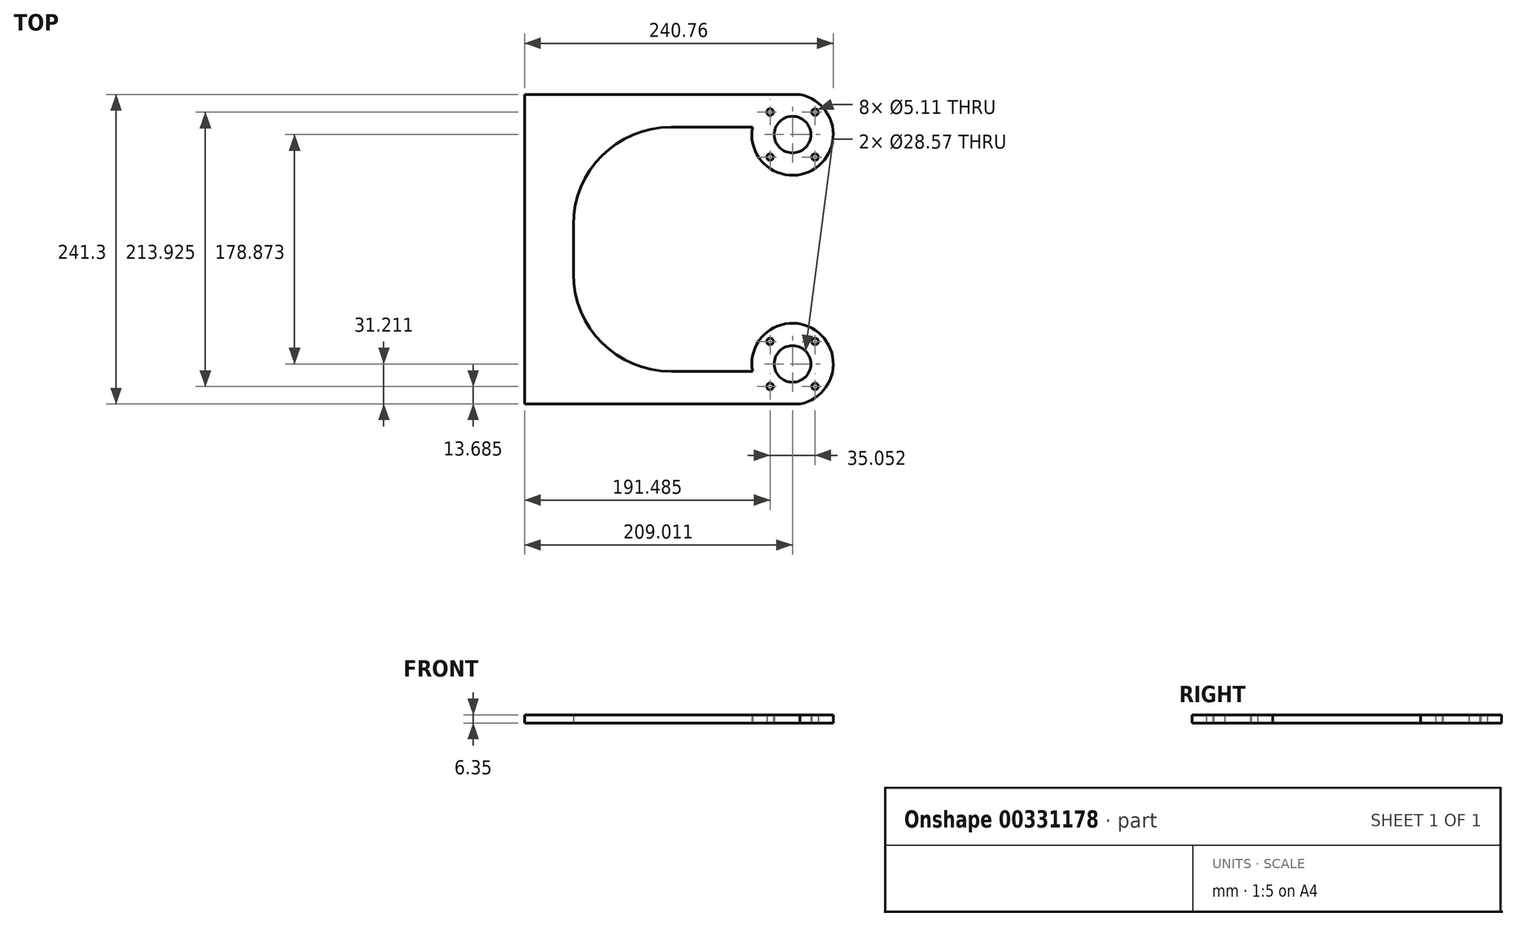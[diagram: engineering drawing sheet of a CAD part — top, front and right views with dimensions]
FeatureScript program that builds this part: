
annotation { "Feature Type Name" : "Feature", "Feature Type Description" : "" }
export const myFeature = defineFeature(function(context is Context, id is Id, definition is map)
    precondition{}
    {
        {
            var Q0;
            Q0=qCreatedBy(makeId("Top.planeOp"),FACE);
            var sketch = newSketch(context, id + "F0", { "sketchPlane" : qUnion([Q0])});
            skCircle(sketch, "E0", {"center": v(0, 0) * mm, "radius": 88.9 * mm, "construction": true});
            skLineSegment(sketch, "E1", {"start": v(60, -118.94) * mm, "end": v(-143.2, -118.94) * mm});
            skLineSegment(sketch, "E2", {"start": v(-143.2, -118.94) * mm, "end": v(-143.2, 122.36) * mm});
            skLineSegment(sketch, "E3", {"start": v(-143.2, 122.36) * mm, "end": v(60, 122.36) * mm});
            skLineSegment(sketch, "E4", {"start": v(34.6, 96.96) * mm, "end": v(-105.1, 96.96) * mm});
            skLineSegment(sketch, "E5", {"start": v(-105.1, 96.96) * mm, "end": v(-105.1, -93.54) * mm});
            skLineSegment(sketch, "E6", {"start": v(-105.1, -93.54) * mm, "end": v(34.6, -93.54) * mm});
            skArc(sketch, "E7", {"start": v(60, -118.94) * mm, "mid": v(88.26, -65.28) * mm, "end": v(34.6, -93.54) * mm});
            skArc(sketch, "E8", {"start": v(34.6, 96.96) * mm, "mid": v(88.26, 68.7) * mm, "end": v(60, 122.36) * mm});
            skCircle(sketch, "E9", {"center": v(65.81, -87.73) * mm, "radius": 36.51 * mm, "construction": true});
            skCircle(sketch, "E10", {"center": v(65.81, 91.14) * mm, "radius": 36.51 * mm, "construction": true});
            skLineSegment(sketch, "E11.bottom", {"start": v(83.34, 108.67) * mm, "end": v(48.28, 108.67) * mm, "construction": true});
            skLineSegment(sketch, "E11.top", {"start": v(83.34, 73.62) * mm, "end": v(48.28, 73.62) * mm, "construction": true});
            skLineSegment(sketch, "E11.left", {"start": v(83.34, 108.67) * mm, "end": v(83.34, 73.62) * mm, "construction": true});
            skLineSegment(sketch, "E11.right", {"start": v(48.28, 108.67) * mm, "end": v(48.28, 73.62) * mm, "construction": true});
            skLineSegment(sketch, "E12.bottom", {"start": v(83.34, -70.2) * mm, "end": v(48.28, -70.2) * mm, "construction": true});
            skLineSegment(sketch, "E12.top", {"start": v(83.34, -105.26) * mm, "end": v(48.28, -105.26) * mm, "construction": true});
            skLineSegment(sketch, "E12.left", {"start": v(83.34, -70.2) * mm, "end": v(83.34, -105.26) * mm, "construction": true});
            skLineSegment(sketch, "E12.right", {"start": v(48.28, -70.2) * mm, "end": v(48.28, -105.26) * mm, "construction": true});
            skCircle(sketch, "E13", {"center": v(83.34, -105.26) * mm, "radius": 2.55 * mm});
            skCircle(sketch, "E14", {"center": v(83.34, -70.2) * mm, "radius": 2.55 * mm});
            skCircle(sketch, "E15", {"center": v(48.28, -70.2) * mm, "radius": 2.55 * mm});
            skCircle(sketch, "E16", {"center": v(48.28, -105.26) * mm, "radius": 2.55 * mm});
            skCircle(sketch, "E17", {"center": v(83.34, 73.62) * mm, "radius": 2.55 * mm});
            skCircle(sketch, "E18", {"center": v(83.34, 108.67) * mm, "radius": 2.55 * mm});
            skCircle(sketch, "E19", {"center": v(48.28, 108.67) * mm, "radius": 2.55 * mm});
            skCircle(sketch, "E20", {"center": v(48.28, 73.62) * mm, "radius": 2.55 * mm});
            skCircle(sketch, "E21", {"center": v(65.81, 91.14) * mm, "radius": 14.29 * mm});
            skCircle(sketch, "E22", {"center": v(65.81, -87.73) * mm, "radius": 14.29 * mm});
            skSolve(sketch);
        }
        {
            var Q0;
            Q0 = qSketchRegion(id + "F0", true);
            extrude(context, id + "F1", {"entities" : qUnion([Q0]), "depth" : 6.35 * mm});
        }
        {
            var Q0;
            Q0=makeQuery(id+"F1.opExtrude","SWEPT_EDGE",EDGE,{"disambiguationData":[OSD([sQuery(id+"F0.wireOp",EDGE,"E4"),sQuery(id+"F0.wireOp",EDGE,"E5")])]});
            fillet(context, id + "F2", {"entities" : qUnion([Q0]), "radius" : 76.2 * mm, "tangentPropagation" : true, "allowEdgeOverflow" : false});
        }
        {
            var Q0;
            Q0=makeQuery(id+"F1.opExtrude","SWEPT_EDGE",EDGE,{"disambiguationData":[OSD([sQuery(id+"F0.wireOp",EDGE,"E5"),sQuery(id+"F0.wireOp",EDGE,"E6")])]});
            fillet(context, id + "F3", {"entities" : qUnion([Q0]), "radius" : 76.2 * mm, "tangentPropagation" : true, "allowEdgeOverflow" : false});
        }
        {
            var Q0;
            Q0=makeQuery(id+"F1.opExtrude","CAP_FACE",FACE,{"disambiguationData":[OSD([sQuery(id+"F0.wireOp",EDGE,"E1"),sQuery(id+"F0.wireOp",EDGE,"E2"),sQuery(id+"F0.wireOp",EDGE,"E3"),sQuery(id+"F0.wireOp",EDGE,"E4"),sQuery(id+"F0.wireOp",EDGE,"E5"),sQuery(id+"F0.wireOp",EDGE,"E6"),sQuery(id+"F0.wireOp",EDGE,"E7"),sQuery(id+"F0.wireOp",EDGE,"E8"),sQuery(id+"F0.wireOp",EDGE,"E13"),sQuery(id+"F0.wireOp",EDGE,"E14"),sQuery(id+"F0.wireOp",EDGE,"E15"),sQuery(id+"F0.wireOp",EDGE,"E16"),sQuery(id+"F0.wireOp",EDGE,"E17"),sQuery(id+"F0.wireOp",EDGE,"E18"),sQuery(id+"F0.wireOp",EDGE,"E19"),sQuery(id+"F0.wireOp",EDGE,"E20"),sQuery(id+"F0.wireOp",EDGE,"E21"),sQuery(id+"F0.wireOp",EDGE,"E22")])],"isStart":false});
            var sketch = newSketch(context, id + "F4", { "sketchPlane" : qUnion([Q0])});
            skLineSegment(sketch, "E23.bottom", {"start": v(60, 122.36) * mm, "end": v(90.4, 122.36) * mm});
            skLineSegment(sketch, "E23.top", {"start": v(60, 129.79) * mm, "end": v(90.4, 129.79) * mm});
            skLineSegment(sketch, "E23.left", {"start": v(60, 122.36) * mm, "end": v(60, 129.79) * mm});
            skLineSegment(sketch, "E23.right", {"start": v(90.4, 122.36) * mm, "end": v(90.4, 129.79) * mm});
            skLineSegment(sketch, "E24.bottom", {"start": v(60, -118.94) * mm, "end": v(90.83, -118.94) * mm});
            skLineSegment(sketch, "E24.top", {"start": v(60, -126.08) * mm, "end": v(90.83, -126.08) * mm});
            skLineSegment(sketch, "E24.left", {"start": v(60, -118.94) * mm, "end": v(60, -126.08) * mm});
            skLineSegment(sketch, "E24.right", {"start": v(90.83, -118.94) * mm, "end": v(90.83, -126.08) * mm});
            skSolve(sketch);
        }
        {
            var Q0;
            Q0 = qSketchRegion(id + "F4", true);
            extrude(context, id + "F5", {"entities" : qUnion([Q0]), "operationType" : NewBodyOperationType.REMOVE, "oppositeDirection" : true, "depth" : 25.4 * mm});
        }
    });
